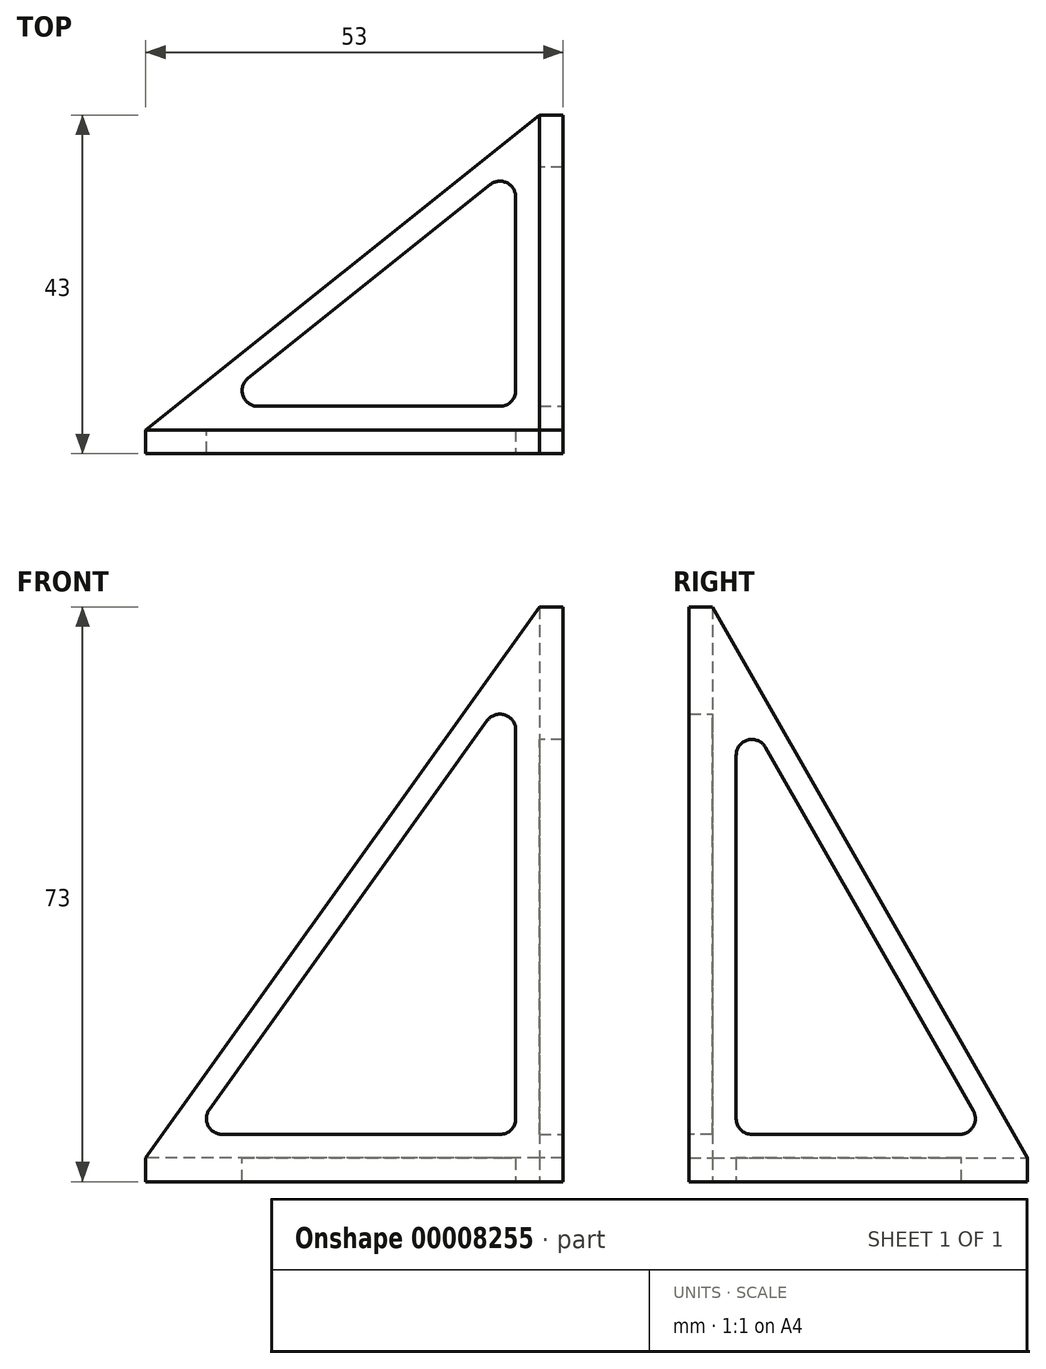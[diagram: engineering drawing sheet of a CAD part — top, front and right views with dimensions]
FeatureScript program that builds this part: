
annotation { "Feature Type Name" : "Feature", "Feature Type Description" : "" }
export const myFeature = defineFeature(function(context is Context, id is Id, definition is map)
    precondition{}
    {
        {
            var Q0;
            Q0=qCreatedBy(makeId("Top.planeOp"),FACE);
            var sketch = newSketch(context, id + "F0", { "sketchPlane" : qUnion([Q0])});
            skLineSegment(sketch, "E0", {"start": v(-3, 0) * mm, "end": v(-53, 0) * mm});
            skLineSegment(sketch, "E1", {"start": v(-53, 0) * mm, "end": v(-53, 3) * mm});
            skLineSegment(sketch, "E2", {"start": v(-53, 3) * mm, "end": v(-3, 3) * mm});
            skLineSegment(sketch, "E3", {"start": v(0, 3) * mm, "end": v(0, 43) * mm});
            skLineSegment(sketch, "E4", {"start": v(0, 43) * mm, "end": v(-3, 43) * mm});
            skLineSegment(sketch, "E5", {"start": v(-3, 43) * mm, "end": v(-3, 3) * mm});
            skLineSegment(sketch, "E6", {"start": v(-3, 0) * mm, "end": v(0, 0) * mm});
            skLineSegment(sketch, "E7", {"start": v(-3, 3) * mm, "end": v(0, 3) * mm});
            skLineSegment(sketch, "E8", {"start": v(0, 3) * mm, "end": v(0, 0) * mm});
            skLineSegment(sketch, "E9", {"start": v(-3, 3) * mm, "end": v(-3, 0) * mm});
            skLineSegment(sketch, "E10", {"start": v(-53, 3) * mm, "end": v(-3, 43) * mm});
            skLineSegment(sketch, "E11", {"start": v(-44.45, 6) * mm, "end": v(-6, 6) * mm});
            skLineSegment(sketch, "E12", {"start": v(-6, 6) * mm, "end": v(-6, 36.76) * mm});
            skLineSegment(sketch, "E13", {"start": v(-6, 36.76) * mm, "end": v(-44.45, 6) * mm});
            skLineSegment(sketch, "E14", {"start": v(-6, 21.38) * mm, "end": v(-3, 21.38) * mm, "construction": true});
            skLineSegment(sketch, "E15", {"start": v(-25.22, 6) * mm, "end": v(-25.22, 3) * mm, "construction": true});
            skLineSegment(sketch, "E16", {"start": v(-25.22, 21.38) * mm, "end": v(-27.1, 23.72) * mm, "construction": true});
            skSolve(sketch);
        }
        {
            var Q0;
            Q0=makeQuery(id+"F0.imprint","IMPRINT",FACE,{"disambiguationData":[TD([[makeQuery(id+"F0.imprint","IMPRINT",EDGE,{"derivedFrom":sQuery(id+"F0.wireOp",EDGE,"E2")}),1.0]])]});
            var Q1;
            Q1=makeQuery(id+"F0.imprint","IMPRINT",FACE,{"disambiguationData":[TD([[makeQuery(id+"F0.imprint","IMPRINT",EDGE,{"derivedFrom":sQuery(id+"F0.wireOp",EDGE,"E0")}),-1.0]])]});
            var Q2;
            Q2=makeQuery(id+"F0.imprint","IMPRINT",FACE,{"disambiguationData":[TD([[makeQuery(id+"F0.imprint","IMPRINT",EDGE,{"derivedFrom":sQuery(id+"F0.wireOp",EDGE,"E6")}),1.0]])]});
            var Q3;
            Q3=makeQuery(id+"F0.imprint","IMPRINT",FACE,{"disambiguationData":[TD([[makeQuery(id+"F0.imprint","IMPRINT",EDGE,{"derivedFrom":sQuery(id+"F0.wireOp",EDGE,"E3")}),1.0]])]});
            extrude(context, id + "F1", {"entities" : qUnion([Q0, Q1, Q2, Q3]), "depth" : 3 * mm});
        }
        {
            var Q0;
            Q0=qCreatedBy(makeId("Right.planeOp"),FACE);
            var sketch = newSketch(context, id + "F2", { "sketchPlane" : qUnion([Q0])});
            skLineSegment(sketch, "E17.0.0", {"start": v(3, 0) * mm, "end": v(43, 0) * mm});
            skLineSegment(sketch, "E17.0.1", {"start": v(43, 0) * mm, "end": v(43, 3) * mm});
            skLineSegment(sketch, "E17.0.2", {"start": v(43, 3) * mm, "end": v(3, 3) * mm});
            skLineSegment(sketch, "E18", {"start": v(0, 3) * mm, "end": v(0, 73) * mm});
            skLineSegment(sketch, "E19", {"start": v(0, 73) * mm, "end": v(3, 73) * mm});
            skLineSegment(sketch, "E20", {"start": v(3, 73) * mm, "end": v(3, 3) * mm});
            skPoint(sketch, "E21", {"position": v(3, 3) * mm});
            skLineSegment(sketch, "E22", {"start": v(3, 3) * mm, "end": v(3, 0) * mm});
            skPoint(sketch, "E17.0.3.end.orphan", {"position": v(0, 0) * mm});
            skLineSegment(sketch, "E23", {"start": v(0, 3) * mm, "end": v(3, 3) * mm});
            skLineSegment(sketch, "E24", {"start": v(0, 3) * mm, "end": v(0, 0) * mm});
            skLineSegment(sketch, "E25", {"start": v(0, 0) * mm, "end": v(3, 0) * mm});
            skLineSegment(sketch, "E26", {"start": v(3, 73) * mm, "end": v(43, 3) * mm});
            skLineSegment(sketch, "E27", {"start": v(6, 6) * mm, "end": v(6, 61.7) * mm});
            skLineSegment(sketch, "E28", {"start": v(6, 61.7) * mm, "end": v(37.83, 6) * mm});
            skLineSegment(sketch, "E29", {"start": v(37.83, 6) * mm, "end": v(6, 6) * mm});
            skPoint(sketch, "E30", {"position": v(6, 33.85) * mm});
            skPoint(sketch, "E31", {"position": v(21.92, 33.85) * mm});
            skPoint(sketch, "E32", {"position": v(21.92, 6) * mm});
            skLineSegment(sketch, "E33", {"start": v(6, 33.85) * mm, "end": v(3, 33.85) * mm, "construction": true});
            skLineSegment(sketch, "E34", {"start": v(21.92, 33.85) * mm, "end": v(24.52, 35.34) * mm, "construction": true});
            skLineSegment(sketch, "E35", {"start": v(21.92, 6) * mm, "end": v(21.92, 3) * mm, "construction": true});
            skSolve(sketch);
        }
        {
            var Q0;
            Q0=makeQuery(id+"F2.imprint","IMPRINT",FACE,{"disambiguationData":[TD([[makeQuery(id+"F2.imprint","IMPRINT",EDGE,{"derivedFrom":sQuery(id+"F2.wireOp",EDGE,"E18")}),-1.0]])]});
            var Q1;
            Q1=makeQuery(id+"F2.imprint","IMPRINT",FACE,{"disambiguationData":[TD([[makeQuery(id+"F2.imprint","IMPRINT",EDGE,{"derivedFrom":sQuery(id+"F2.wireOp",EDGE,"E17.0.2")}),-1.0]])]});
            extrude(context, id + "F3", {"entities" : qUnion([Q0, Q1]), "operationType" : NewBodyOperationType.ADD, "oppositeDirection" : true, "depth" : 3 * mm});
        }
        {
            var Q0;
            Q0=qCreatedBy(makeId("Front.planeOp"),FACE);
            var sketch = newSketch(context, id + "F4", { "sketchPlane" : qUnion([Q0])});
            skLineSegment(sketch, "E36.0.0", {"start": v(-53, 0) * mm, "end": v(0, 0) * mm});
            skLineSegment(sketch, "E36.0.1", {"start": v(0, 0) * mm, "end": v(0, 73) * mm});
            skLineSegment(sketch, "E36.0.2", {"start": v(0, 73) * mm, "end": v(-3, 73) * mm});
            skLineSegment(sketch, "E36.0.3", {"start": v(-3, 73) * mm, "end": v(-3, 3) * mm});
            skLineSegment(sketch, "E36.0.4", {"start": v(-3, 3) * mm, "end": v(-53, 3) * mm});
            skLineSegment(sketch, "E36.0.5", {"start": v(-53, 3) * mm, "end": v(-53, 0) * mm});
            skLineSegment(sketch, "E37", {"start": v(-53, 3) * mm, "end": v(-3, 73) * mm});
            skLineSegment(sketch, "E38", {"start": v(-6, 6) * mm, "end": v(-6, 63.64) * mm});
            skLineSegment(sketch, "E39", {"start": v(-6, 63.64) * mm, "end": v(-47.17, 6) * mm});
            skLineSegment(sketch, "E40", {"start": v(-47.17, 6) * mm, "end": v(-6, 6) * mm});
            skPoint(sketch, "E41", {"position": v(-26.59, 6) * mm});
            skPoint(sketch, "E42", {"position": v(-6, 34.82) * mm});
            skPoint(sketch, "E43", {"position": v(-26.59, 34.82) * mm});
            skLineSegment(sketch, "E44", {"start": v(-26.59, 34.82) * mm, "end": v(-29.03, 36.56) * mm, "construction": true});
            skLineSegment(sketch, "E45", {"start": v(-26.59, 6) * mm, "end": v(-26.59, 3) * mm, "construction": true});
            skLineSegment(sketch, "E46", {"start": v(-6, 34.82) * mm, "end": v(-3, 34.82) * mm, "construction": true});
            skLineSegment(sketch, "E47", {"start": v(-3, 3) * mm, "end": v(-3, 0) * mm, "construction": true});
            skSolve(sketch);
        }
        {
            var Q0;
            Q0=makeQuery(id+"F4.imprint","IMPRINT",FACE,{"disambiguationData":[TD([[makeQuery(id+"F4.imprint","IMPRINT",EDGE,{"derivedFrom":sQuery(id+"F4.wireOp",EDGE,"E36.0.3")}),-1.0]])]});
            extrude(context, id + "F5", {"entities" : qUnion([Q0]), "operationType" : NewBodyOperationType.ADD, "oppositeDirection" : true, "depth" : 3 * mm});
        }
        {
            var Q0;
            Q0=makeQuery(id+"F5.opExtrude","CAP_EDGE",EDGE,{"disambiguationData":[OSD([sQuery(id+"F4.wireOp",EDGE,"E36.0.4")])],"isStart":false});
            var Q1;
            Q1=makeQuery(id+"F5.opExtrude","CAP_EDGE",EDGE,{"disambiguationData":[OSD([sQuery(id+"F4.wireOp",EDGE,"E36.0.3")])],"isStart":false});
            var Q2;
            Q2=makeQuery(id+"F3.opExtrude","CAP_EDGE",EDGE,{"disambiguationData":[OSD([sQuery(id+"F2.wireOp",EDGE,"E17.0.2"),sQuery(id+"F2.wireOp",EDGE,"E23")])],"isStart":false});
            var Q3;
            Q3=makeQuery(id+"F3.opExtrude","SWEPT_EDGE",EDGE,{"disambiguationData":[OSD([sQuery(id+"F2.wireOp",EDGE,"E27"),sQuery(id+"F2.wireOp",EDGE,"E29")])]});
            var Q4;
            Q4=makeQuery(id+"F5.opExtrude","SWEPT_EDGE",EDGE,{"disambiguationData":[OSD([sQuery(id+"F4.wireOp",EDGE,"E38"),sQuery(id+"F4.wireOp",EDGE,"E40")])]});
            var Q5;
            Q5=makeQuery(id+"F1.opExtrude","SWEPT_EDGE",EDGE,{"disambiguationData":[OSD([sQuery(id+"F0.wireOp",EDGE,"E11"),sQuery(id+"F0.wireOp",EDGE,"E12")])]});
            var Q6;
            Q6=makeQuery(id+"F5.opExtrude","SWEPT_EDGE",EDGE,{"disambiguationData":[OSD([sQuery(id+"F4.wireOp",EDGE,"E38"),sQuery(id+"F4.wireOp",EDGE,"E39")])]});
            var Q7;
            Q7=makeQuery(id+"F3.opExtrude","SWEPT_EDGE",EDGE,{"disambiguationData":[OSD([sQuery(id+"F2.wireOp",EDGE,"E27"),sQuery(id+"F2.wireOp",EDGE,"E28")])]});
            var Q8;
            Q8=makeQuery(id+"F3.opExtrude","SWEPT_EDGE",EDGE,{"disambiguationData":[OSD([sQuery(id+"F2.wireOp",EDGE,"E28"),sQuery(id+"F2.wireOp",EDGE,"E29")])]});
            var Q9;
            Q9=makeQuery(id+"F1.opExtrude","SWEPT_EDGE",EDGE,{"disambiguationData":[OSD([sQuery(id+"F0.wireOp",EDGE,"E12"),sQuery(id+"F0.wireOp",EDGE,"E13")])]});
            var Q10;
            Q10=makeQuery(id+"F5.opExtrude","SWEPT_EDGE",EDGE,{"disambiguationData":[OSD([sQuery(id+"F4.wireOp",EDGE,"E39"),sQuery(id+"F4.wireOp",EDGE,"E40")])]});
            var Q11;
            Q11=makeQuery(id+"F1.opExtrude","SWEPT_EDGE",EDGE,{"disambiguationData":[OSD([sQuery(id+"F0.wireOp",EDGE,"E11"),sQuery(id+"F0.wireOp",EDGE,"E13")])]});
            fillet(context, id + "F6", {"entities" : qUnion([Q0, Q1, Q2, Q3, Q4, Q5, Q6, Q7, Q8, Q9, Q10, Q11]), "radius" : 2 * mm, "tangentPropagation" : true, "allowEdgeOverflow" : false});
        }
    });
